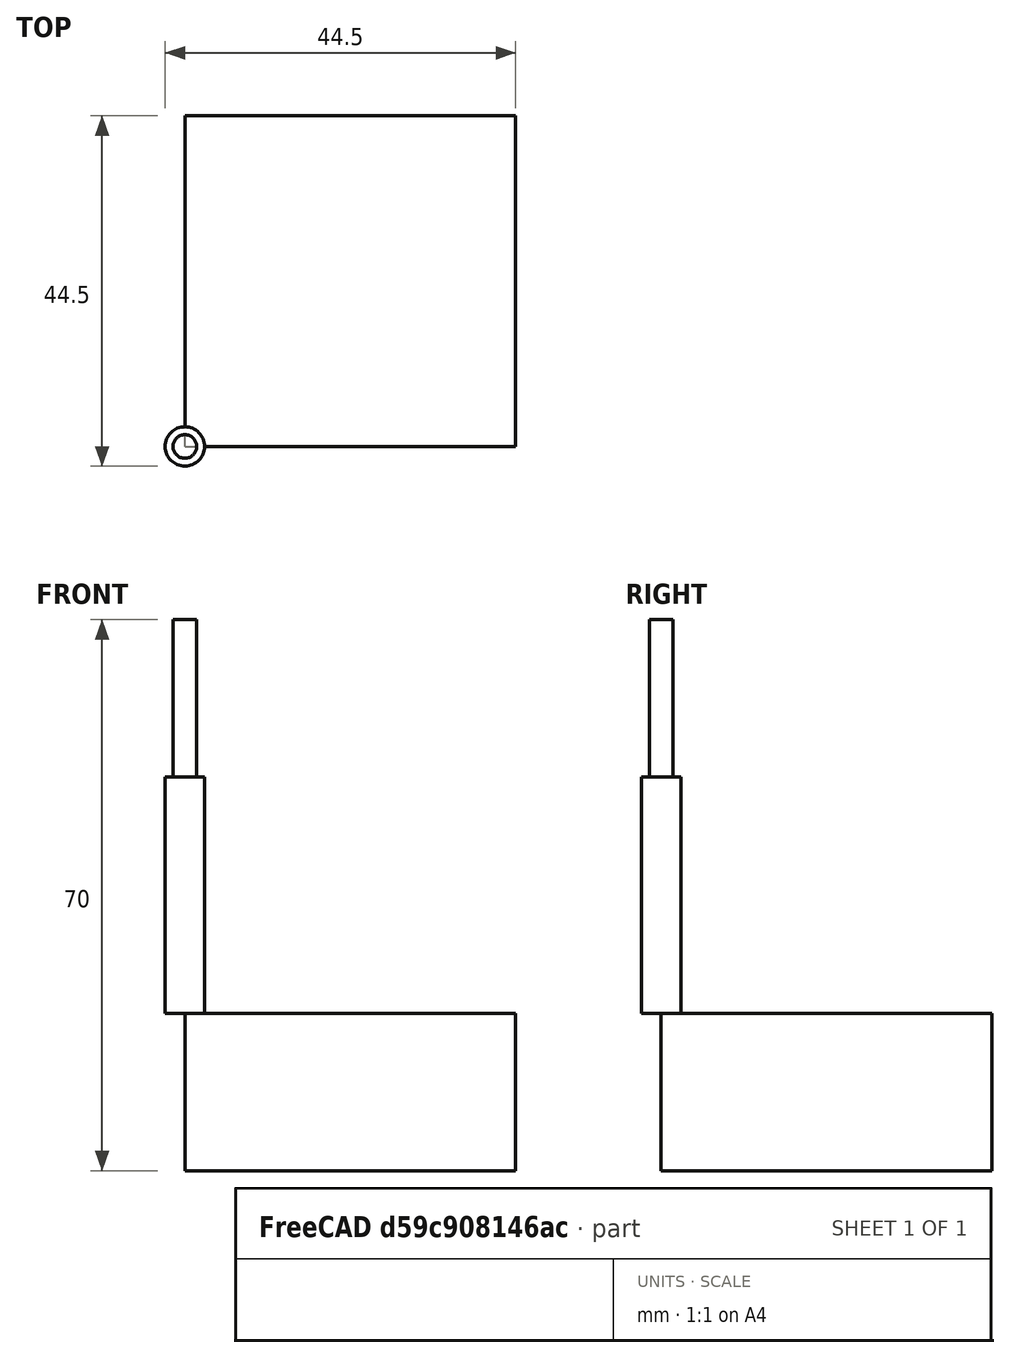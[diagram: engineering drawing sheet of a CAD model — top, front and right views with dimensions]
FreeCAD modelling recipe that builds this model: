
FCSTD DOCUMENT  (FreeCAD 0.19R23546 (Git))
Label: GabariPercage25-6
License: All rights reserved
LicenseURL: http://en.wikipedia.org/wiki/All_rights_reserved
objects: Path::FeaturePython×4, Sketcher::SketchObject×3, Part::FeaturePython×3, PartDesign::Pocket×2, PartDesign::Pad×1, PartDesign::Body×1, App::FeaturePython×1, App::DocumentObjectGroup×1, Path::FeatureCompoundPython×1, Mesh::FeaturePython×1
note: 15 computed .brp shape members not serialized (recipe doc carries the construction recipe); baked Part::Feature solids carry a one-line shape summary decoded from their .brp

FEATURE [Sketcher::SketchObject] Sketch
  MapMode = 5
  Support = -> [XY_Plane]
  sketch-geometry (4):
    g0: LineSegment StartX=0 StartY=40 StartZ=0 EndX=40 EndY=40 EndZ=0
    g1: LineSegment StartX=40 StartY=40 StartZ=0 EndX=40 EndY=0 EndZ=0
    g2: LineSegment StartX=40 StartY=0 StartZ=0 EndX=0 EndY=0 EndZ=0
    g3: LineSegment StartX=0 StartY=0 StartZ=0 EndX=0 EndY=40 EndZ=0
  constraints (10):
    c: Coincident(g0,g1)
    c: Coincident(g1,g2)
    c: Coincident(g2,g3)
    c: Coincident(g3,g0)
    c: Horizontal(g0)
    c: Horizontal(g2)
    c: Vertical(g1)
    c: Vertical(g3)
    c: PointOnObject(g0,g-2)
    c: PointOnObject(g1,g-1)
FEATURE [PartDesign::Pad] Pad
  Direction = (1,1,1)
  Length = 20
  Length2 = 100
  Profile = -> Sketch
  Type = 0
FEATURE [Sketcher::SketchObject] Sketch001
  MapMode = 5
  Placement = pos=(0,0,20) rot=(0,0,1;0rad)
  Support = -> [Pad]
  sketch-geometry (1):
    g0: Circle CenterX=20 CenterY=20 CenterZ=0 NormalX=0 NormalY=0 NormalZ=1 AngleXU=0 Radius=3.05
  constraints (1):
    c: Diameter(g0) = 6.1
FEATURE [PartDesign::Pocket] Pocket
  BaseFeature = -> Pad
  Length = 15
  Length2 = 100
  Profile = -> Sketch001
  Type = 0
FEATURE [Sketcher::SketchObject] Sketch002
  MapMode = 5
  Placement = pos=(0,0,20) rot=(0,0,1;0rad)
  Support = -> [Pocket]
  sketch-geometry (1):
    g0: Circle CenterX=20 CenterY=20 CenterZ=0 NormalX=0 NormalY=0 NormalZ=1 AngleXU=0 Radius=12.5
  constraints (1):
    c: Diameter(g0) = 25
FEATURE [PartDesign::Pocket] Pocket001
  BaseFeature = -> Pocket
  Length = 8
  Length2 = 100
  Profile = -> Sketch002
  Type = 0
FEATURE [PartDesign::Body] Body
  Group = -> [Sketch,Pad,Sketch001,Pocket,Sketch002,Pocket001]
  Origin = -> Origin
  Tip = -> Pocket001
FEATURE [App::FeaturePython] SetupSheet  # Path/CAM operation (typed FeaturePython)
  ClearanceHeightExpression = OpStockZMax+SetupSheet.ClearanceHeightOffset
  ClearanceHeightOffset = 5
  CoolantMode = 0
  CoolantModes = None | Flood | Mist
  FinalDepthExpression = OpFinalDepth
  HorizRapid = 0
  SafeHeightExpression = OpStockZMax+SetupSheet.SafeHeightOffset
  SafeHeightOffset = 3
  StartDepthExpression = OpStartDepth
  StepDownExpression = OpToolDiameter
  VertRapid = 0
FEATURE [Part::FeaturePython] Clone  label="Model-Body"  # Draft clone (typed FeaturePython)
  AttacherType = Attacher::AttachEngine3D
  Fuse = false
  Objects = -> [Body]
  PathResource = Model
  Placement = pos=(1,1,-20) rot=(0,0,1;0rad)
  Scale = (1,1,1)
FEATURE [App::DocumentObjectGroup] Model
  Group = -> [Clone]
FEATURE [Part::FeaturePython] ToolBit  label="Endmill"  # Path/CAM toolbit (typed FeaturePython)
  BitShape = <path>
  CuttingEdgeHeight = 30
  Diameter = 6
  Length = 50
  ShankDiameter = 3
  ShapeName = endmill
FEATURE [Path::FeaturePython] TC__Default_Tool  label="TC: Default Tool"  # Path/CAM operation (typed FeaturePython)
  HorizFeed = 0
  HorizRapid = 0
  SpindleDir = 0
  SpindleSpeed = 0
  Tool = -> ToolBit
  ToolNumber = 1
  VertFeed = 0
  VertRapid = 0
  expr: VertRapid = SetupSheet.VertRapid
  expr: HorizRapid = SetupSheet.HorizRapid
FEATURE [Part::FeaturePython] Stock  # WARN: FeaturePython — macro-defined, semantics opaque (R4)
  Base = -> Model
  ExtXneg = 1
  ExtXpos = 1
  ExtYneg = 1
  ExtYpos = 1
  ExtZneg = 0
  ExtZpos = 0
  Placement = pos=(1,1,-20) rot=(0,0,1;0rad)
  StockType = FromBase
FEATURE [Path::FeaturePython] Pocket_Shape  # Path/CAM operation (typed FeaturePython)
  Active = true
  AreaParams:
    Tolerance = 1e-07
    FitArcs = True
    Simplify = False
    CleanDistance = 0.0
    Accuracy = 0.01
    Unit = 1.0
    MinArcPoints = 4
    MaxArcPoints = 100
    ClipperScale = 10000000.0
    Fill = 0
    Coplanar = 0
    Reorient = True
    Outline = False
    Explode = False
    OpenMode = 0
    Deflection = 0.01
    SubjectFill = 0
    ClipFill = 0
    Offset = 0.0
    ExtraPass = 0
    Stepover = 0.0
    LastStepover = 0.0
    JoinType = 0
    EndType = 0
    MiterLimit = 2.0
    RoundPrecision = 0.0
    PocketMode = 4
    ToolRadius = 3.0
    PocketExtraOffset = 0.0
    PocketStepover = 6.0
    PocketLastStepover = 0.0
    FromCenter = True
    Angle = 45.0
    AngleShift = 0.0
    Shift = 0.0
    Thicken = False
    SectionCount = -1
    Stepdown = 1.0
    SectionOffset = 0.0
    SectionTolerance = 1e-06
    SectionMode = 2
    Project = False
  AttemptInverseAngle = true
  Base = -> [Clone]
  ClearanceHeight = 5
  CoolantMode = None
  CutMode = 0
  CycleTime = Erreur de temps de cycle
  EnableRotation = 0
  ExtensionCorners = true
  ExtensionFeature = -> [Clone]
  ExtensionLengthDefault = 3
  ExtraOffset = 0
  FinalDepth = -8
  FinishDepth = 0
  InverseAngle = false
  KeepToolDown = false
  LimitDepthToFace = true
  MinTravel = false
  OffsetPattern = 3
  OpFinalDepth = -8
  OpStartDepth = 0
  OpStockZMax = 0
  OpStockZMin = -20
  OpToolDiameter = 6
  PathParams = {'orientation': 1, 'feedrate': 0.0, 'feedrate_v': 0.0, 'verbose': True, 'resume_height': 3.0, 'retraction': 5.0, 'return_end': True, 'preamble': False, 'start': Vector (25.48981778207899, 16.304019437590462, 5.0)}
  ReverseDirection = false
  SafeHeight = 3
  StartAt = 0
  StartDepth = 0
  StartPoint = (0,0,0)
  StepDown = 3
  StepOver = 100
  ToolController = -> TC__Default_Tool
  UseOutline = false
  UseStartPoint = true
  ZigZagAngle = 45
  expr: StartDepth = OpStartDepth
  expr: FinalDepth = OpFinalDepth
  expr: StepDown = 3
  expr: SafeHeight = OpStockZMax + SetupSheet.SafeHeightOffset
  expr: ClearanceHeight = OpStockZMax + SetupSheet.ClearanceHeightOffset
  expr: ExtensionLengthDefault = OpToolDiameter / 2
FEATURE [Path::FeaturePython] Profile  # Path/CAM operation (typed FeaturePython)
  Active = true
  AreaParams:
    Tolerance = 1e-07
    FitArcs = True
    Simplify = False
    CleanDistance = 0.0
    Accuracy = 0.01
    Unit = 1.0
    MinArcPoints = 4
    MaxArcPoints = 100
    ClipperScale = 10000000.0
    Fill = 0
    Coplanar = 0
    Reorient = True
    Outline = False
    Explode = False
    OpenMode = 0
    Deflection = 0.01
    SubjectFill = 0
    ClipFill = 0
    Offset = -3.0
    ExtraPass = 0
    Stepover = 0.0
    LastStepover = 0.0
    JoinType = 0
    EndType = 0
    MiterLimit = 2.0
    RoundPrecision = 0.0
    PocketMode = 0
    ToolRadius = 1.0
    PocketExtraOffset = 0.0
    PocketStepover = 0.0
    PocketLastStepover = 0.0
    FromCenter = False
    Angle = 45.0
    AngleShift = 0.0
    Shift = 0.0
    Thicken = False
    SectionCount = -1
    Stepdown = 1.0
    SectionOffset = 0.0
    SectionTolerance = 1e-06
    SectionMode = 2
    Project = False
  AttemptInverseAngle = true
  Base = -> [Clone]
  ClearanceHeight = 5
  CoolantMode = None
  CycleTime = Erreur de temps de cycle
  Direction = 1
  EnableRotation = 0
  ExpandProfile = 0
  ExpandProfileStepOver = 100
  FinalDepth = -15
  HandleMultipleFeatures = 1
  InverseAngle = false
  JoinType = 0
  LimitDepthToFace = true
  MiterLimit = 0.1
  OffsetExtra = 0
  OpFinalDepth = -15
  OpStartDepth = 0
  OpStockZMax = 0
  OpStockZMin = -20
  OpToolDiameter = 6
  PathParams = {'orientation': 0, 'feedrate': 0.0, 'feedrate_v': 0.0, 'verbose': True, 'resume_height': 3.0, 'retraction': 5.0, 'return_end': True, 'preamble': False, 'start': Vector (0.0, 0.0, 0.0)}
  ReverseDirection = false
  SafeHeight = 3
  Side = 1
  StartDepth = 0
  StartPoint = (0,0,0)
  StepDown = 3
  ToolController = -> TC__Default_Tool
  UseComp = true
  UseStartPoint = true
  processCircles = false
  processHoles = false
  processPerimeter = true
  expr: StartDepth = OpStartDepth
  expr: FinalDepth = OpFinalDepth
  expr: StepDown = 3
  expr: SafeHeight = OpStockZMax + SetupSheet.SafeHeightOffset
  expr: ClearanceHeight = OpStockZMax + SetupSheet.ClearanceHeightOffset
FEATURE [Path::FeatureCompoundPython] Operations  # Path/CAM operation (typed FeaturePython)
  Group = -> [Pocket_Shape,Profile]
  UsePlacements = false
FEATURE [Path::FeaturePython] Job  # Path/CAM operation (typed FeaturePython)
  CycleTime = 00:00:00
  Fixtures = G54
  GeometryTolerance = 0.01
  LastPostProcessDate = 2021-04-13 13:08:41.650577
  LastPostProcessOutput = <userpath>/dev/CNC/MiscCNC/FixationsCNC/GabariPercage25-6.gcode
  Model = -> Model
  Operations = -> Operations
  OrderOutputBy = 0
  PostProcessor = 13
  PostProcessorOutputFile = <userpath>/dev/CNC/MiscCNC/FixationsCNC/GabariPercage25-6.gcode
  SetupSheet = -> SetupSheet
  SplitOutput = false
  Stock = -> Stock
  ToolController = -> [TC__Default_Tool]
FEATURE [Mesh::FeaturePython] CutMaterial  # WARN: FeaturePython — macro-defined, semantics opaque (R4)
note: 1 file-system path scrubbed to <path> (originals preserved in the JSON sidecar)
